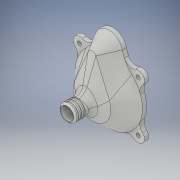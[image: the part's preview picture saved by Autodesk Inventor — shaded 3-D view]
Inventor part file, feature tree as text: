
AUTODESK INVENTOR PART (.ipt)
format: ipt  version: 2018 (Build 220112000, 112)  size: 827,392 bytes
history: native  units: in
note: dims shown in document units (in); Inventor stores cm internally (conversion verified against a paired STEP export)
features: sketch x7, plane x5, extrude x5, fillet x4, projected_geometry x3, loft x2, shell x2, mirror x1, pattern_linear x1, chamfer x1, other x1
ambient origin geometry x8: Origin, YZ Plane, XZ Plane, XY Plane, X Axis, Y Axis, Z Axis, Center Point
bodies: Body1 (feature_tree)
feature tree (32):
  sketch  "Sketch2"  dims[d4=4.0in d5=0.825in]
  plane  "Work Plane2"
  loft  "Loft2"
  extrude  "Extrusion1"  Depth=2.0in
  plane  "Work Plane5"
  loft  "Loft6"
  shell  "Shell3"  Thickness=1.125in
  sketch  "Sketch20"  dims[d25=0.25in d26=0.0in d41=0.1in d42=0.75in d55=0.5in]
  extrude  "Extrusion4"  TaperAngle=0.0deg  [1 undecoded]
  extrude  "Extrusion5"  Depth=0.1in
  fillet  "Fillet3"  Radius=0.75in
  fillet  "Fillet4"  Radius=0.5in
  extrude  "Extrusion6"  TaperAngle=0.0deg  [1 undecoded]
  fillet  "Fillet5"  [1 undecoded]
  mirror  "Mirror1"
  fillet  "Fillet6"  Radius=0.1in
  plane  "Work Plane6"
  extrude  "Extrusion7"  Depth=0.1in TaperAngle=0.0deg
  pattern_linear  "Rectangular Pattern1"  Spacing1=1.0in  [1 undecoded]
  chamfer  "Chamfer1"  Distance=0.5in
  shell  "Shell1"  Thickness=0.5in
  plane  "Work Plane3"
  plane  "Work Plane4"
  sketch  "Sketch7"  dims[d6=2.25in d7=2.0in]
  sketch  "Sketch8"  dims[d18=1.0in d19=0.25in d20=1.125in]
  projected_geometry  "Projected Loop1"
  sketch  "Sketch19"  dims[d21=0.0in d22=90.0deg d23=0.0in d24=90.0deg]
  other  "Edges6"
  projected_geometry  "Projected Loop6"
  sketch  "Sketch21"  dims[d56=1.0in d57=0.0in d58=90.0deg d59=0.0in d60=90.0deg d61=0.1in]
  projected_geometry  "Projected Loop7"
  sketch  "Sketch22"  dims[d63=0.125in d64=1.0in d65=0.0in d66=1.0in d67=0.0in d68=0.5in d69=0.5in d70=1.75in d71=1.5in d72=1.75in d73=1.5in d74=0.25in d75=0.25in d76=0.25in d77=0.0in d78=0.5in d79=0.5in d80=-0.1in d81=0.95in d82=0.1in d83=0.0in d84=1.1811in d86=0.2in d87=0.1in d88=0.125in d89=45.0deg]
note: 4 required parameter values undecoded (feature->parameter linkage not recoverable at this tier; creation-order binding heuristic only, values carry confidence <= 0.55)
